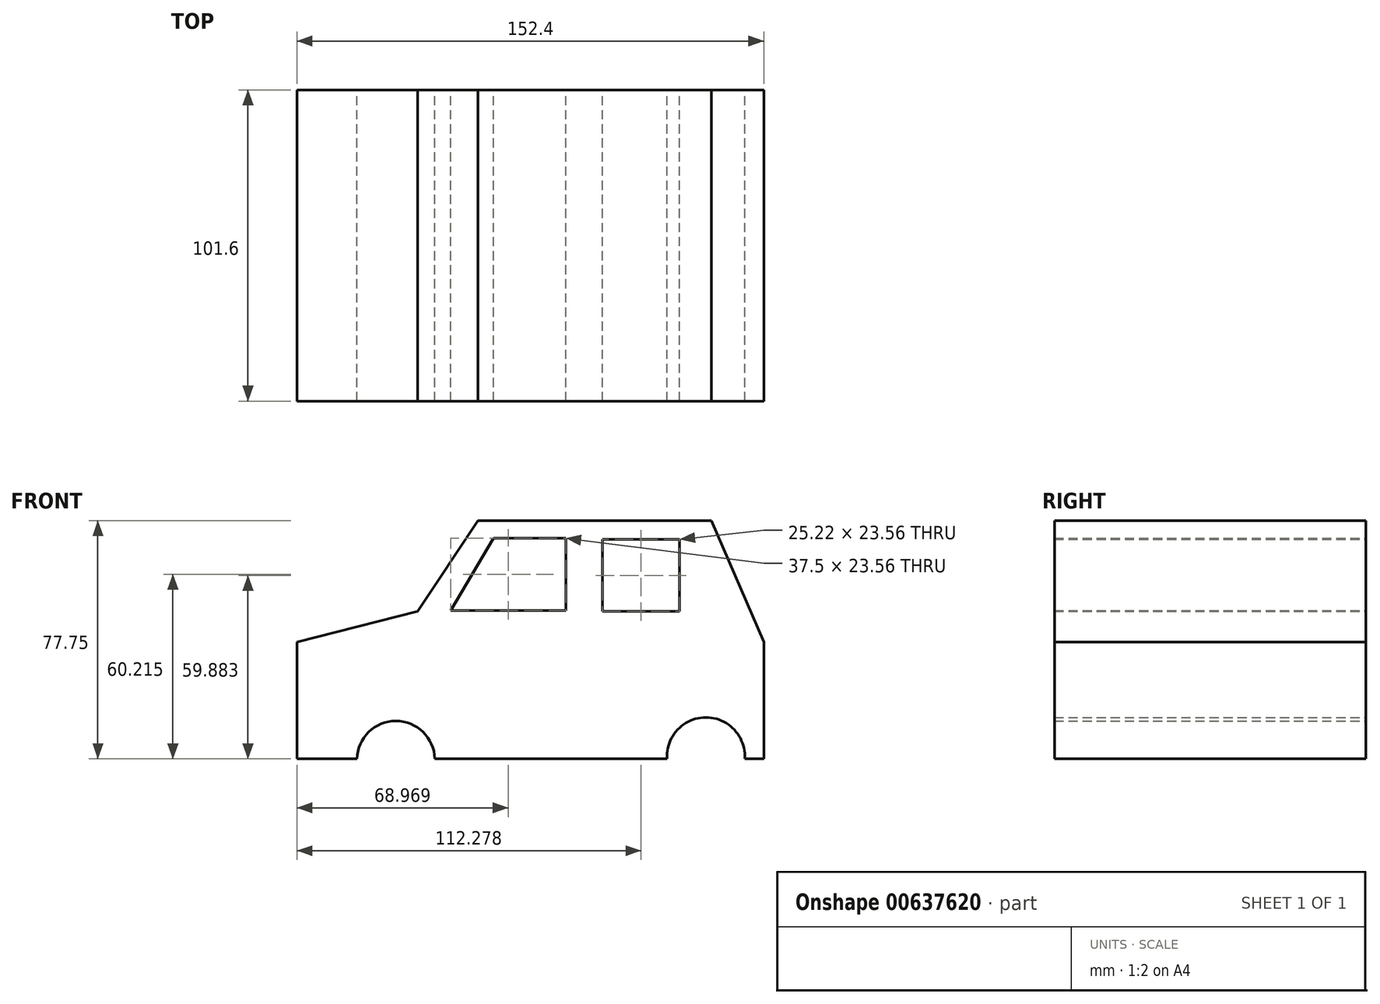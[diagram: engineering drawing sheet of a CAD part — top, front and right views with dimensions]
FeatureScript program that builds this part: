
annotation { "Feature Type Name" : "Feature", "Feature Type Description" : "" }
export const myFeature = defineFeature(function(context is Context, id is Id, definition is map)
    precondition{}
    {
        {
            var Q0;
            Q0=qCreatedBy(makeId("Front.planeOp"),FACE);
            var sketch = newSketch(context, id + "F0", { "sketchPlane" : qUnion([Q0])});
            skLineSegment(sketch, "E0", {"start": v(-145.28, 46.42) * mm, "end": v(-145.28, 8.32) * mm});
            skLineSegment(sketch, "E1", {"start": v(-145.28, 8.32) * mm, "end": v(7.12, 8.32) * mm});
            skLineSegment(sketch, "E2", {"start": v(7.12, 8.32) * mm, "end": v(7.12, 46.42) * mm});
            skLineSegment(sketch, "E3", {"start": v(7.12, 46.42) * mm, "end": v(-9.97, 86.07) * mm});
            skLineSegment(sketch, "E4", {"start": v(-9.97, 86.07) * mm, "end": v(-86.17, 86.07) * mm});
            skLineSegment(sketch, "E5", {"start": v(-86.17, 86.07) * mm, "end": v(-105.85, 56.46) * mm});
            skLineSegment(sketch, "E6", {"start": v(-105.85, 56.46) * mm, "end": v(-145.28, 46.42) * mm});
            skSolve(sketch);
        }
        {
            var Q0;
            Q0 = qSketchRegion(id + "F0", true);
            extrude(context, id + "F1", {"entities" : qUnion([Q0]), "depth" : 101.6 * mm, "offsetDistance" : 25.4 * mm});
        }
        {
            var Q0;
            Q0=qCreatedBy(makeId("Front.planeOp"),FACE);
            var sketch = newSketch(context, id + "F2", { "sketchPlane" : qUnion([Q0])});
            skLineSegment(sketch, "E7", {"start": v(-95.06, 56.75) * mm, "end": v(-81.12, 80.32) * mm});
            skLineSegment(sketch, "E8", {"start": v(-81.12, 80.32) * mm, "end": v(-57.56, 80.32) * mm});
            skLineSegment(sketch, "E9", {"start": v(-57.56, 80.32) * mm, "end": v(-57.56, 56.75) * mm});
            skLineSegment(sketch, "E10", {"start": v(-57.56, 56.75) * mm, "end": v(-95.06, 56.75) * mm});
            skSolve(sketch);
        }
        {
            var Q0;
            Q0 = qSketchRegion(id + "F2", true);
            extrude(context, id + "F3", {"entities" : qUnion([Q0]), "operationType" : NewBodyOperationType.REMOVE, "depth" : 115.06 * mm, "offsetDistance" : 25.4 * mm});
        }
        {
            var Q0;
            Q0=qCreatedBy(makeId("Front.planeOp"),FACE);
            var sketch = newSketch(context, id + "F4", { "sketchPlane" : qUnion([Q0])});
            skLineSegment(sketch, "E11", {"start": v(-45.61, 56.42) * mm, "end": v(-45.61, 79.98) * mm});
            skLineSegment(sketch, "E12", {"start": v(-45.61, 79.98) * mm, "end": v(-20.4, 79.98) * mm});
            skLineSegment(sketch, "E13", {"start": v(-20.4, 79.98) * mm, "end": v(-20.4, 56.42) * mm});
            skLineSegment(sketch, "E14", {"start": v(-20.4, 56.42) * mm, "end": v(-45.61, 56.42) * mm});
            skSolve(sketch);
        }
        {
            var Q0;
            Q0 = qSketchRegion(id + "F4", true);
            extrude(context, id + "F5", {"entities" : qUnion([Q0]), "operationType" : NewBodyOperationType.REMOVE, "depth" : 158 * mm, "offsetDistance" : 25.4 * mm});
        }
        {
            var Q0;
            Q0=qCreatedBy(makeId("Front.planeOp"),FACE);
            var sketch = newSketch(context, id + "F6", { "sketchPlane" : qUnion([Q0])});
            skCircle(sketch, "E15", {"center": v(-112.98, 7.97) * mm, "radius": 12.7 * mm});
            skSolve(sketch);
        }
        {
            var Q0;
            Q0 = qSketchRegion(id + "F6", true);
            extrude(context, id + "F7", {"entities" : qUnion([Q0]), "operationType" : NewBodyOperationType.REMOVE, "depth" : 195.83 * mm, "offsetDistance" : 25.4 * mm});
        }
        {
            var Q0;
            Q0=qCreatedBy(makeId("Front.planeOp"),FACE);
            var sketch = newSketch(context, id + "F8", { "sketchPlane" : qUnion([Q0])});
            skCircle(sketch, "E16", {"center": v(-11.8, 9.14) * mm, "radius": 12.7 * mm});
            skSolve(sketch);
        }
        {
            var Q0;
            Q0 = qSketchRegion(id + "F8", true);
            extrude(context, id + "F9", {"entities" : qUnion([Q0]), "operationType" : NewBodyOperationType.REMOVE, "depth" : 145.54 * mm, "offsetDistance" : 25.4 * mm});
        }
    });
